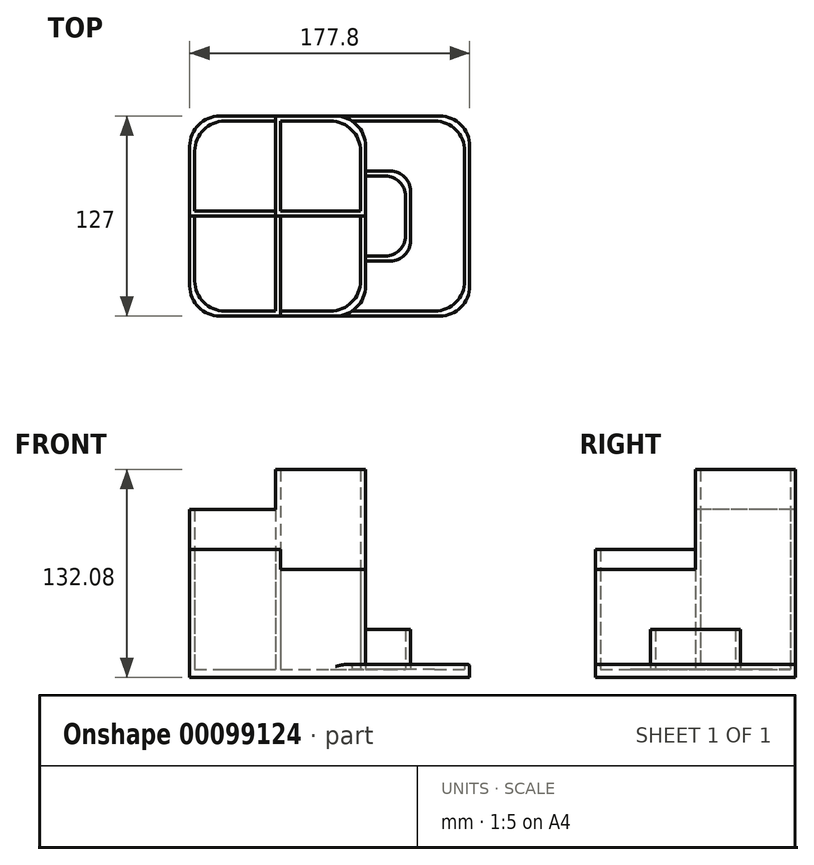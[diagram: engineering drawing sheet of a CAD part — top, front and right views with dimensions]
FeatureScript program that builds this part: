
annotation { "Feature Type Name" : "Feature", "Feature Type Description" : "" }
export const myFeature = defineFeature(function(context is Context, id is Id, definition is map)
    precondition{}
    {
        {
            var Q0;
            Q0=qCreatedBy(makeId("Top.planeOp"),FACE);
            var sketch = newSketch(context, id + "F0", { "sketchPlane" : qUnion([Q0])});
            skLineSegment(sketch, "E0.bottom", {"start": v(19.05, 0) * mm, "end": v(158.75, 0) * mm});
            skLineSegment(sketch, "E0.top", {"start": v(19.05, -127) * mm, "end": v(158.75, -127) * mm});
            skLineSegment(sketch, "E0.left", {"start": v(0, -19.05) * mm, "end": v(0, -107.95) * mm});
            skLineSegment(sketch, "E0.right", {"start": v(177.8, -19.05) * mm, "end": v(177.8, -107.95) * mm});
            skPoint(sketch, "E1.visualSharp", {"position": v(0, 0) * mm});
            skArc(sketch, "E1.filletArc", {"start": v(19.05, 0) * mm, "mid": v(5.58, -5.58) * mm, "end": v(0, -19.05) * mm});
            skPoint(sketch, "E2.visualSharp", {"position": v(0, -127) * mm});
            skArc(sketch, "E2.filletArc", {"start": v(0, -107.95) * mm, "mid": v(5.58, -121.42) * mm, "end": v(19.05, -127) * mm});
            skPoint(sketch, "E3.visualSharp", {"position": v(177.8, -127) * mm});
            skArc(sketch, "E3.filletArc", {"start": v(158.75, -127) * mm, "mid": v(172.22, -121.42) * mm, "end": v(177.8, -107.95) * mm});
            skPoint(sketch, "E4.visualSharp", {"position": v(177.8, 0) * mm});
            skArc(sketch, "E4.filletArc", {"start": v(177.8, -19.05) * mm, "mid": v(172.22, -5.58) * mm, "end": v(158.75, 0) * mm});
            skSolve(sketch);
        }
        {
            var Q0;
            Q0 = qSketchRegion(id + "F0", true);
            extrude(context, id + "F1", {"entities" : qUnion([Q0]), "depth" : 5.08 * mm});
        }
        {
            var Q0;
            Q0=makeQuery(id+"F1.opExtrude","CAP_FACE",FACE,{"disambiguationData":[OSD([sQuery(id+"F0.wireOp",EDGE,"E0.bottom"),sQuery(id+"F0.wireOp",EDGE,"E0.top"),sQuery(id+"F0.wireOp",EDGE,"E0.left"),sQuery(id+"F0.wireOp",EDGE,"E0.right"),sQuery(id+"F0.wireOp",EDGE,"E1.filletArc"),sQuery(id+"F0.wireOp",EDGE,"E2.filletArc"),sQuery(id+"F0.wireOp",EDGE,"E3.filletArc"),sQuery(id+"F0.wireOp",EDGE,"E4.filletArc")])],"isStart":false});
            var sketch = newSketch(context, id + "F2", { "sketchPlane" : qUnion([Q0])});
            skLineSegment(sketch, "E5.bottom", {"start": v(19.05, 0) * mm, "end": v(158.75, 0) * mm});
            skLineSegment(sketch, "E5.top", {"start": v(19.05, -127) * mm, "end": v(158.75, -127) * mm});
            skLineSegment(sketch, "E5.left", {"start": v(0, -19.05) * mm, "end": v(0, -107.95) * mm});
            skLineSegment(sketch, "E5.right", {"start": v(177.8, -19.05) * mm, "end": v(177.8, -107.95) * mm});
            skPoint(sketch, "E6.visualSharp", {"position": v(0, 0) * mm});
            skArc(sketch, "E6.filletArc", {"start": v(19.05, 0) * mm, "mid": v(5.58, -5.58) * mm, "end": v(0, -19.05) * mm});
            skPoint(sketch, "E7.visualSharp", {"position": v(177.8, -127) * mm});
            skArc(sketch, "E7.filletArc", {"start": v(158.75, -127) * mm, "mid": v(172.22, -121.42) * mm, "end": v(177.8, -107.95) * mm});
            skPoint(sketch, "E8.visualSharp", {"position": v(0, -127) * mm});
            skArc(sketch, "E8.filletArc", {"start": v(0, -107.95) * mm, "mid": v(5.58, -121.42) * mm, "end": v(19.05, -127) * mm});
            skPoint(sketch, "E9.visualSharp", {"position": v(177.8, 0) * mm});
            skArc(sketch, "E9.filletArc", {"start": v(177.8, -19.05) * mm, "mid": v(172.22, -5.58) * mm, "end": v(158.75, 0) * mm});
            skLineSegment(sketch, "E10.bottom", {"start": v(22.23, -3.18) * mm, "end": v(54.43, -3.18) * mm});
            skLineSegment(sketch, "E10.left", {"start": v(3.17, -22.23) * mm, "end": v(3.18, -60.32) * mm});
            skPoint(sketch, "E11.visualSharp", {"position": v(3.17, -3.18) * mm});
            skArc(sketch, "E11.filletArc", {"start": v(22.23, -3.18) * mm, "mid": v(8.75, -8.75) * mm, "end": v(3.18, -22.22) * mm});
            skLineSegment(sketch, "E12", {"start": v(54.43, -3.18) * mm, "end": v(54.43, -60.32) * mm});
            skLineSegment(sketch, "E13", {"start": v(54.43, -60.32) * mm, "end": v(3.18, -60.32) * mm});
            skLineSegment(sketch, "E14", {"start": v(0, -63.5) * mm, "end": v(57.6, -63.5) * mm});
            skLineSegment(sketch, "E15", {"start": v(57.6, -63.5) * mm, "end": v(57.6, 0) * mm});
            skSolve(sketch);
        }
        {
            var Q0;
            {var subQ0=sQuery(id+"F2.wireOp",EDGE,"E6.filletArc");Q0=makeQuery(id+"F2.imprint","IMPRINT",FACE,{"disambiguationData":[TD([[makeQuery(id+"F2.imprint","IMPRINT",EDGE,{"derivedFrom":subQ0}),1.0]])]});}
            extrude(context, id + "F3", {"entities" : qUnion([Q0]), "operationType" : NewBodyOperationType.ADD, "depth" : 101.6 * mm});
        }
        {
            var Q0;
            {var subQ0=sQuery(id+"F0.wireOp",EDGE,"E4.filletArc");var subQ1=sQuery(id+"F0.wireOp",EDGE,"E3.filletArc");var subQ2=sQuery(id+"F0.wireOp",EDGE,"E2.filletArc");var subQ3=sQuery(id+"F0.wireOp",EDGE,"E0.bottom");var subQ4=sQuery(id+"F0.wireOp",EDGE,"E0.top");var subQ5=sQuery(id+"F0.wireOp",EDGE,"E0.left");var subQ6=sQuery(id+"F0.wireOp",EDGE,"E0.right");Q0=makeQuery(id+"F3.boolean.opBoolean","SPLIT",FACE,{"disambiguationData":[TD([makeQuery(id+"F1.opExtrude","SWEPT_FACE",FACE,{"disambiguationData":[OSD([subQ3])]})])],"derivedFrom":makeQuery(id+"F1.opExtrude","CAP_FACE",FACE,{"disambiguationData":[OSD([subQ3,subQ4,subQ5,subQ6,sQuery(id+"F0.wireOp",EDGE,"E1.filletArc"),subQ2,subQ1,subQ0])],"isStart":false})});}
            var sketch = newSketch(context, id + "F4", { "sketchPlane" : qUnion([Q0])});
            skLineSegment(sketch, "E16", {"start": v(0, -63.5) * mm, "end": v(0, -107.95) * mm});
            skLineSegment(sketch, "E17", {"start": v(19.05, -127) * mm, "end": v(57.6, -127) * mm});
            skLineSegment(sketch, "E18", {"start": v(57.6, -127) * mm, "end": v(57.6, -63.5) * mm});
            skLineSegment(sketch, "E19", {"start": v(57.6, -63.5) * mm, "end": v(0, -63.5) * mm});
            skPoint(sketch, "E20.visualSharp", {"position": v(0, -127) * mm});
            skArc(sketch, "E20.filletArc", {"start": v(0, -107.95) * mm, "mid": v(5.58, -121.42) * mm, "end": v(19.05, -127) * mm});
            skLineSegment(sketch, "E21", {"start": v(3.17, -63.5) * mm, "end": v(3.18, -104.78) * mm});
            skLineSegment(sketch, "E22", {"start": v(22.23, -123.83) * mm, "end": v(54.43, -123.83) * mm});
            skLineSegment(sketch, "E23", {"start": v(54.43, -123.83) * mm, "end": v(54.43, -63.5) * mm});
            skPoint(sketch, "E24.visualSharp", {"position": v(3.18, -123.83) * mm});
            skArc(sketch, "E24.filletArc", {"start": v(3.18, -104.78) * mm, "mid": v(8.75, -118.25) * mm, "end": v(22.23, -123.82) * mm});
            skSolve(sketch);
        }
        {
            var Q0;
            {var subQ1=sQuery(id+"F4.wireOp",EDGE,"E16");Q0=makeQuery(id+"F4.imprint","IMPRINT",FACE,{"disambiguationData":[TD([[makeQuery(id+"F4.imprint","IMPRINT",EDGE,{"derivedFrom":subQ1}),1.0]])]});}
            extrude(context, id + "F5", {"entities" : qUnion([Q0]), "operationType" : NewBodyOperationType.ADD, "depth" : 76.2 * mm});
        }
        {
            var Q0;
            {var subQ0=sQuery(id+"F0.wireOp",EDGE,"E0.right");var subQ4=sQuery(id+"F0.wireOp",EDGE,"E3.filletArc");var subQ6=sQuery(id+"F0.wireOp",EDGE,"E0.top");var subQ8=sQuery(id+"F0.wireOp",EDGE,"E0.bottom");var subQ9=makeQuery(id+"F1.opExtrude","SWEPT_FACE",FACE,{"disambiguationData":[OSD([subQ8])]});var subQ10=sQuery(id+"F0.wireOp",EDGE,"E4.filletArc");var subQ12=sQuery(id+"F0.wireOp",EDGE,"E2.filletArc");var subQ13=sQuery(id+"F0.wireOp",EDGE,"E0.left");Q0=makeQuery(id+"F5.boolean.opBoolean","SPLIT",FACE,{"disambiguationData":[TD([subQ9])],"derivedFrom":makeQuery(id+"F3.boolean.opBoolean","SPLIT",FACE,{"disambiguationData":[TD([subQ9])],"derivedFrom":makeQuery(id+"F1.opExtrude","CAP_FACE",FACE,{"disambiguationData":[OSD([subQ8,subQ6,subQ13,subQ0,sQuery(id+"F0.wireOp",EDGE,"E1.filletArc"),subQ12,subQ4,subQ10])],"isStart":false})})});}
            var sketch = newSketch(context, id + "F6", { "sketchPlane" : qUnion([Q0])});
            skPoint(sketch, "E25.firstSnap0", {"position": v(57.6, -63.5) * mm});
            skLineSegment(sketch, "E25.bottom", {"start": v(54.43, -63.5) * mm, "end": v(111.58, -63.5) * mm});
            skLineSegment(sketch, "E25.top", {"start": v(54.43, 0) * mm, "end": v(92.53, 0) * mm});
            skLineSegment(sketch, "E25.left", {"start": v(54.43, -63.5) * mm, "end": v(54.43, 0) * mm});
            skLineSegment(sketch, "E25.right", {"start": v(111.58, -63.5) * mm, "end": v(111.58, -19.05) * mm});
            skLineSegment(sketch, "E26.top", {"start": v(57.6, -60.33) * mm, "end": v(108.4, -60.33) * mm});
            skLineSegment(sketch, "E26.left", {"start": v(57.6, 0) * mm, "end": v(57.6, -60.33) * mm});
            skLineSegment(sketch, "E27", {"start": v(108.4, -60.32) * mm, "end": v(108.4, -22.23) * mm});
            skLineSegment(sketch, "E28", {"start": v(89.35, -3.17) * mm, "end": v(57.6, -3.18) * mm});
            skPoint(sketch, "E29.visualSharp", {"position": v(108.4, -3.17) * mm});
            skArc(sketch, "E29.filletArc", {"start": v(108.4, -22.23) * mm, "mid": v(102.82, -8.75) * mm, "end": v(89.35, -3.18) * mm});
            skPoint(sketch, "E30.visualSharp", {"position": v(111.58, 0) * mm});
            skArc(sketch, "E30.filletArc", {"start": v(111.58, -19.05) * mm, "mid": v(106, -5.58) * mm, "end": v(92.53, 0) * mm});
            skSolve(sketch);
        }
        {
            var Q0;
            Q0 = qSketchRegion(id + "F6", true);
            extrude(context, id + "F7", {"entities" : qUnion([Q0]), "operationType" : NewBodyOperationType.ADD, "depth" : 127 * mm});
        }
        {
            var Q0;
            {var subQ2=sQuery(id+"F0.wireOp",EDGE,"E4.filletArc");var subQ4=sQuery(id+"F0.wireOp",EDGE,"E0.bottom");var subQ5=makeQuery(id+"F1.opExtrude","SWEPT_FACE",FACE,{"disambiguationData":[OSD([subQ4])]});var subQ7=sQuery(id+"F0.wireOp",EDGE,"E0.top");var subQ10=sQuery(id+"F0.wireOp",EDGE,"E3.filletArc");var subQ13=sQuery(id+"F0.wireOp",EDGE,"E0.right");var subQ15=sQuery(id+"F0.wireOp",EDGE,"E2.filletArc");var subQ16=sQuery(id+"F0.wireOp",EDGE,"E0.left");Q0=makeQuery(id+"F7.boolean.opBoolean","SPLIT",FACE,{"disambiguationData":[TD([subQ5])],"derivedFrom":makeQuery(id+"F5.boolean.opBoolean","SPLIT",FACE,{"disambiguationData":[TD([subQ5])],"derivedFrom":makeQuery(id+"F3.boolean.opBoolean","SPLIT",FACE,{"disambiguationData":[TD([subQ5])],"derivedFrom":makeQuery(id+"F1.opExtrude","CAP_FACE",FACE,{"disambiguationData":[OSD([subQ4,subQ7,subQ16,subQ13,sQuery(id+"F0.wireOp",EDGE,"E1.filletArc"),subQ15,subQ10,subQ2])],"isStart":false})})})});}
            var sketch = newSketch(context, id + "F8", { "sketchPlane" : qUnion([Q0])});
            skLineSegment(sketch, "E31.bottom", {"start": v(54.43, -60.32) * mm, "end": v(111.58, -60.32) * mm});
            skLineSegment(sketch, "E31.top", {"start": v(54.43, -127) * mm, "end": v(92.53, -127) * mm});
            skLineSegment(sketch, "E31.left", {"start": v(54.43, -60.32) * mm, "end": v(54.43, -127) * mm});
            skLineSegment(sketch, "E31.right", {"start": v(111.58, -60.32) * mm, "end": v(111.58, -107.95) * mm});
            skLineSegment(sketch, "E32.bottom", {"start": v(57.6, -63.5) * mm, "end": v(108.4, -63.5) * mm});
            skLineSegment(sketch, "E32.top", {"start": v(57.6, -123.83) * mm, "end": v(89.35, -123.83) * mm});
            skLineSegment(sketch, "E32.left", {"start": v(57.6, -63.5) * mm, "end": v(57.6, -123.83) * mm});
            skLineSegment(sketch, "E32.right", {"start": v(108.4, -63.5) * mm, "end": v(108.4, -104.78) * mm});
            skPoint(sketch, "E33.visualSharp", {"position": v(108.4, -123.83) * mm});
            skArc(sketch, "E33.filletArc", {"start": v(89.35, -123.83) * mm, "mid": v(102.82, -118.25) * mm, "end": v(108.4, -104.78) * mm});
            skPoint(sketch, "E34.visualSharp", {"position": v(111.58, -127) * mm});
            skArc(sketch, "E34.filletArc", {"start": v(92.53, -127) * mm, "mid": v(106, -121.42) * mm, "end": v(111.58, -107.95) * mm});
            skSolve(sketch);
        }
        {
            var Q0;
            Q0 = qSketchRegion(id + "F8", true);
            extrude(context, id + "F9", {"entities" : qUnion([Q0]), "operationType" : NewBodyOperationType.ADD, "depth" : 63.5 * mm});
        }
        {
            var Q0;
            {var subQ3=sQuery(id+"F0.wireOp",EDGE,"E4.filletArc");var subQ5=sQuery(id+"F0.wireOp",EDGE,"E0.bottom");var subQ6=makeQuery(id+"F1.opExtrude","SWEPT_FACE",FACE,{"disambiguationData":[OSD([subQ5])]});var subQ9=sQuery(id+"F0.wireOp",EDGE,"E0.top");var subQ11=sQuery(id+"F0.wireOp",EDGE,"E3.filletArc");var subQ13=sQuery(id+"F0.wireOp",EDGE,"E0.right");var subQ18=sQuery(id+"F0.wireOp",EDGE,"E2.filletArc");var subQ19=sQuery(id+"F0.wireOp",EDGE,"E0.left");Q0=makeQuery(id+"F9.boolean.opBoolean","SPLIT",FACE,{"disambiguationData":[TD([subQ6])],"derivedFrom":makeQuery(id+"F7.boolean.opBoolean","SPLIT",FACE,{"disambiguationData":[TD([subQ6])],"derivedFrom":makeQuery(id+"F5.boolean.opBoolean","SPLIT",FACE,{"disambiguationData":[TD([subQ6])],"derivedFrom":makeQuery(id+"F3.boolean.opBoolean","SPLIT",FACE,{"disambiguationData":[TD([subQ6])],"derivedFrom":makeQuery(id+"F1.opExtrude","CAP_FACE",FACE,{"disambiguationData":[OSD([subQ5,subQ9,subQ19,subQ13,sQuery(id+"F0.wireOp",EDGE,"E1.filletArc"),subQ18,subQ11,subQ3])],"isStart":false})})})})});}
            var sketch = newSketch(context, id + "F10", { "sketchPlane" : qUnion([Q0])});
            skLineSegment(sketch, "E35", {"start": v(92.53, 0) * mm, "end": v(158.75, 0) * mm});
            skLineSegment(sketch, "E36", {"start": v(177.8, -19.05) * mm, "end": v(177.8, -107.95) * mm});
            skLineSegment(sketch, "E37", {"start": v(158.75, -127) * mm, "end": v(92.53, -127) * mm});
            skLineSegment(sketch, "E38", {"start": v(103.06, -3.18) * mm, "end": v(155.58, -3.18) * mm});
            skLineSegment(sketch, "E39", {"start": v(174.62, -22.22) * mm, "end": v(174.62, -104.78) * mm});
            skLineSegment(sketch, "E40", {"start": v(155.58, -123.83) * mm, "end": v(103.06, -123.83) * mm});
            skPoint(sketch, "E41.visualSharp", {"position": v(174.62, -3.18) * mm});
            skArc(sketch, "E41.filletArc", {"start": v(174.63, -22.22) * mm, "mid": v(169.05, -8.75) * mm, "end": v(155.58, -3.17) * mm});
            skPoint(sketch, "E42.visualSharp", {"position": v(177.8, 0) * mm});
            skArc(sketch, "E42.filletArc", {"start": v(177.8, -19.05) * mm, "mid": v(172.22, -5.58) * mm, "end": v(158.75, 0) * mm});
            skPoint(sketch, "E43.visualSharp", {"position": v(174.62, -123.83) * mm});
            skArc(sketch, "E43.filletArc", {"start": v(155.58, -123.83) * mm, "mid": v(169.05, -118.25) * mm, "end": v(174.63, -104.78) * mm});
            skPoint(sketch, "E44.visualSharp", {"position": v(177.8, -127) * mm});
            skArc(sketch, "E44.filletArc", {"start": v(158.75, -127) * mm, "mid": v(172.22, -121.42) * mm, "end": v(177.8, -107.95) * mm});
            skLineSegment(sketch, "E45", {"start": v(92.53, -127) * mm, "end": v(103.06, -123.83) * mm});
            skLineSegment(sketch, "E46", {"start": v(92.53, 0) * mm, "end": v(103.06, -3.18) * mm});
            skSolve(sketch);
        }
        {
            var Q0;
            Q0 = qSketchRegion(id + "F10", true);
            extrude(context, id + "F11", {"entities" : qUnion([Q0]), "operationType" : NewBodyOperationType.ADD, "depth" : 3.17 * mm});
        }
        {
            var Q0;
            Q0=makeQuery(id+"F11.opExtrude","CAP_EDGE",EDGE,{"disambiguationData":[OSD([sQuery(id+"F10.wireOp",EDGE,"E35")])],"isStart":false});
            var Q1;
            Q1=makeQuery(id+"F11.opExtrude","CAP_EDGE",EDGE,{"disambiguationData":[OSD([sQuery(id+"F10.wireOp",EDGE,"E41.filletArc")])],"isStart":false});
            var Q2;
            Q2=makeQuery(id+"F11.opExtrude","CAP_EDGE",EDGE,{"disambiguationData":[OSD([sQuery(id+"F10.wireOp",EDGE,"E42.filletArc")])],"isStart":false});
            var Q3;
            Q3=makeQuery(id+"F11.opExtrude","CAP_EDGE",EDGE,{"disambiguationData":[OSD([sQuery(id+"F10.wireOp",EDGE,"E36")])],"isStart":false});
            var Q4;
            Q4=makeQuery(id+"F11.opExtrude","CAP_EDGE",EDGE,{"disambiguationData":[OSD([sQuery(id+"F10.wireOp",EDGE,"E39")])],"isStart":false});
            var Q5;
            Q5=makeQuery(id+"F11.opExtrude","CAP_EDGE",EDGE,{"disambiguationData":[OSD([sQuery(id+"F10.wireOp",EDGE,"E44.filletArc")])],"isStart":false});
            var Q6;
            Q6=makeQuery(id+"F11.opExtrude","CAP_EDGE",EDGE,{"disambiguationData":[OSD([sQuery(id+"F10.wireOp",EDGE,"E43.filletArc")])],"isStart":false});
            var Q7;
            Q7=makeQuery(id+"F11.opExtrude","CAP_EDGE",EDGE,{"disambiguationData":[OSD([sQuery(id+"F10.wireOp",EDGE,"E40")])],"isStart":false});
            var Q8;
            Q8=makeQuery(id+"F11.opExtrude","CAP_EDGE",EDGE,{"disambiguationData":[OSD([sQuery(id+"F10.wireOp",EDGE,"E37")])],"isStart":false});
            var Q9;
            Q9=makeQuery(id+"F11.opExtrude","CAP_EDGE",EDGE,{"disambiguationData":[OSD([sQuery(id+"F10.wireOp",EDGE,"E38")])],"isStart":false});
            fillet(context, id + "F12", {"entities" : qUnion([Q0, Q1, Q2, Q3, Q4, Q5, Q6, Q7, Q8, Q9]), "radius" : 1.27 * mm, "tangentPropagation" : true, "allowEdgeOverflow" : false});
        }
        {
            var Q0;
            {var subQ3=sQuery(id+"F0.wireOp",EDGE,"E4.filletArc");var subQ5=sQuery(id+"F0.wireOp",EDGE,"E0.bottom");var subQ6=makeQuery(id+"F1.opExtrude","SWEPT_FACE",FACE,{"disambiguationData":[OSD([subQ5])]});var subQ9=sQuery(id+"F0.wireOp",EDGE,"E0.top");var subQ11=sQuery(id+"F0.wireOp",EDGE,"E3.filletArc");var subQ13=sQuery(id+"F0.wireOp",EDGE,"E0.right");var subQ18=sQuery(id+"F0.wireOp",EDGE,"E2.filletArc");var subQ19=sQuery(id+"F0.wireOp",EDGE,"E0.left");Q0=makeQuery(id+"F9.boolean.opBoolean","SPLIT",FACE,{"disambiguationData":[TD([subQ6])],"derivedFrom":makeQuery(id+"F7.boolean.opBoolean","SPLIT",FACE,{"disambiguationData":[TD([subQ6])],"derivedFrom":makeQuery(id+"F5.boolean.opBoolean","SPLIT",FACE,{"disambiguationData":[TD([subQ6])],"derivedFrom":makeQuery(id+"F3.boolean.opBoolean","SPLIT",FACE,{"disambiguationData":[TD([subQ6])],"derivedFrom":makeQuery(id+"F1.opExtrude","CAP_FACE",FACE,{"disambiguationData":[OSD([subQ5,subQ9,subQ19,subQ13,sQuery(id+"F0.wireOp",EDGE,"E1.filletArc"),subQ18,subQ11,subQ3])],"isStart":false})})})})});}
            var sketch = newSketch(context, id + "F13", { "sketchPlane" : qUnion([Q0])});
            skLineSegment(sketch, "E47.bottom", {"start": v(127.45, -92.08) * mm, "end": v(111.58, -92.08) * mm});
            skLineSegment(sketch, "E47.top", {"start": v(127.45, -34.92) * mm, "end": v(111.58, -34.92) * mm});
            skLineSegment(sketch, "E47.left", {"start": v(140.15, -79.38) * mm, "end": v(140.15, -47.62) * mm});
            skLineSegment(sketch, "E47.right", {"start": v(111.58, -92.08) * mm, "end": v(111.58, -34.92) * mm});
            skLineSegment(sketch, "E48.bottom", {"start": v(111.58, -88.9) * mm, "end": v(124.28, -88.9) * mm});
            skLineSegment(sketch, "E48.top", {"start": v(111.58, -38.1) * mm, "end": v(124.28, -38.1) * mm});
            skLineSegment(sketch, "E48.left", {"start": v(111.58, -88.9) * mm, "end": v(111.58, -38.1) * mm});
            skLineSegment(sketch, "E48.right", {"start": v(136.98, -76.2) * mm, "end": v(136.98, -50.8) * mm});
            skPoint(sketch, "E49.visualSharp", {"position": v(136.98, -88.9) * mm});
            skArc(sketch, "E49.filletArc", {"start": v(124.28, -88.9) * mm, "mid": v(133.26, -85.18) * mm, "end": v(136.98, -76.2) * mm});
            skPoint(sketch, "E50.visualSharp", {"position": v(136.98, -38.1) * mm});
            skArc(sketch, "E50.filletArc", {"start": v(136.98, -50.8) * mm, "mid": v(133.26, -41.82) * mm, "end": v(124.28, -38.1) * mm});
            skPoint(sketch, "E51.visualSharp", {"position": v(140.15, -34.92) * mm});
            skArc(sketch, "E51.filletArc", {"start": v(140.15, -47.62) * mm, "mid": v(136.43, -38.64) * mm, "end": v(127.45, -34.92) * mm});
            skPoint(sketch, "E52.visualSharp", {"position": v(140.15, -92.08) * mm});
            skArc(sketch, "E52.filletArc", {"start": v(127.45, -92.08) * mm, "mid": v(136.43, -88.36) * mm, "end": v(140.15, -79.38) * mm});
            skLineSegment(sketch, "E53", {"start": v(116.12, -92.08) * mm, "end": v(116.12, -123.83) * mm, "construction": true});
            skLineSegment(sketch, "E54", {"start": v(115.92, -34.92) * mm, "end": v(115.92, -3.18) * mm, "construction": true});
            skSolve(sketch);
        }
        {
            var Q0;
            {var subQ6=sQuery(id+"F13.wireOp",EDGE,"E47.bottom");Q0=makeQuery(id+"F13.imprint","IMPRINT",FACE,{"disambiguationData":[TD([[makeQuery(id+"F13.imprint","IMPRINT",EDGE,{"derivedFrom":subQ6}),-1.0]])]});}
            extrude(context, id + "F14", {"entities" : qUnion([Q0]), "operationType" : NewBodyOperationType.ADD, "depth" : 25.4 * mm});
        }
    });
